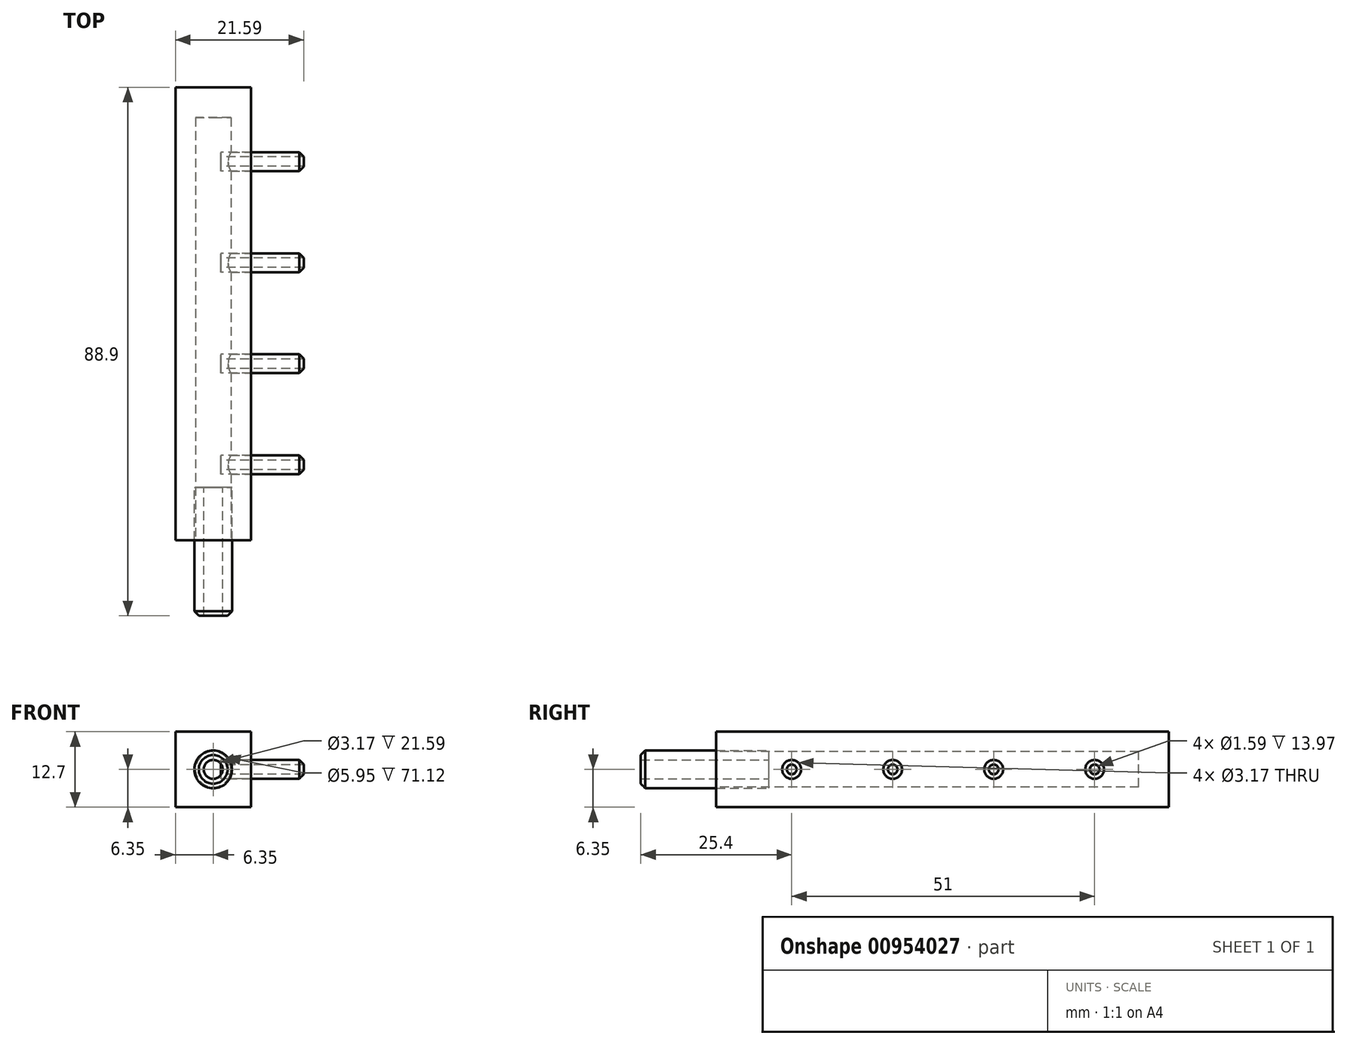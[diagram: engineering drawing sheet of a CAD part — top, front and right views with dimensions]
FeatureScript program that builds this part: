
annotation { "Feature Type Name" : "Feature", "Feature Type Description" : "" }
export const myFeature = defineFeature(function(context is Context, id is Id, definition is map)
    precondition{}
    {
        {
            var Q0;
            Q0=qCreatedBy(makeId("Front.planeOp"),FACE);
            var sketch = newSketch(context, id + "F0", { "sketchPlane" : qUnion([Q0])});
            skLineSegment(sketch, "E0.bottom", {"start": v(6.35, 6.35) * mm, "end": v(-6.35, 6.35) * mm});
            skLineSegment(sketch, "E0.top", {"start": v(6.35, -6.35) * mm, "end": v(-6.35, -6.35) * mm});
            skLineSegment(sketch, "E0.left", {"start": v(6.35, 6.35) * mm, "end": v(6.35, -6.35) * mm});
            skLineSegment(sketch, "E0.right", {"start": v(-6.35, 6.35) * mm, "end": v(-6.35, -6.35) * mm});
            skPoint(sketch, "E0.middle", {"position": v(0, 0) * mm});
            skSolve(sketch);
        }
        {
            var Q0;
            Q0 = qSketchRegion(id + "F0", true);
            extrude(context, id + "F1", {"entities" : qUnion([Q0]), "endBound" : BoundingType.SYMMETRIC, "depth" : 76.2 * mm, "offsetDistance" : 25.4 * mm});
        }
        {
            var Q0;
            Q0=makeQuery(id+"F1.opExtrude","CAP_FACE",FACE,{"disambiguationData":[OSD([sQuery(id+"F0.wireOp",EDGE,"E0.bottom"),sQuery(id+"F0.wireOp",EDGE,"E0.top"),sQuery(id+"F0.wireOp",EDGE,"E0.left"),sQuery(id+"F0.wireOp",EDGE,"E0.right")])],"isStart":false});
            var sketch = newSketch(context, id + "F2", { "sketchPlane" : qUnion([Q0])});
            skCircle(sketch, "E1", {"center": v(0, 0) * mm, "radius": 2.98 * mm});
            skSolve(sketch);
        }
        {
            var Q0;
            Q0 = qSketchRegion(id + "F2", true);
            extrude(context, id + "F3", {"entities" : qUnion([Q0]), "operationType" : NewBodyOperationType.REMOVE, "oppositeDirection" : true, "depth" : 71.12 * mm, "offsetDistance" : 25.4 * mm});
        }
        {
            var Q0;
            Q0=makeQuery(id+"F1.opExtrude","SWEPT_FACE",FACE,{"disambiguationData":[OSD([sQuery(id+"F0.wireOp",EDGE,"E0.left")])]});
            var sketch = newSketch(context, id + "F4", { "sketchPlane" : qUnion([Q0])});
            skCircle(sketch, "E2", {"center": v(-25.4, 0) * mm, "radius": 1.59 * mm});
            skCircle(sketch, "E3.1.0.0", {"center": v(-8.4, 0) * mm, "radius": 1.59 * mm});
            skCircle(sketch, "E3.2.0.0", {"center": v(8.6, 0) * mm, "radius": 1.59 * mm});
            skCircle(sketch, "E3.3.0.0", {"center": v(25.6, 0) * mm, "radius": 1.59 * mm});
            skLineSegment(sketch, "E3.direction1", {"start": v(-25.4, 0) * mm, "end": v(-8.4, 0) * mm, "construction": true});
            skSolve(sketch);
        }
        {
            var Q0;
            Q0 = qSketchRegion(id + "F4", true);
            extrude(context, id + "F5", {"entities" : qUnion([Q0]), "operationType" : NewBodyOperationType.REMOVE, "endBound" : BoundingType.UP_TO_NEXT, "oppositeDirection" : true, "depth" : 25.4 * mm, "offsetDistance" : 25.4 * mm});
        }
        {
            var Q0;
            Q0=makeQuery(id+"F1.opExtrude","CAP_FACE",FACE,{"disambiguationData":[OSD([sQuery(id+"F0.wireOp",EDGE,"E0.bottom"),sQuery(id+"F0.wireOp",EDGE,"E0.top"),sQuery(id+"F0.wireOp",EDGE,"E0.left"),sQuery(id+"F0.wireOp",EDGE,"E0.right")])],"isStart":false});
            var sketch = newSketch(context, id + "F6", { "sketchPlane" : qUnion([Q0])});
            skCircle(sketch, "E4", {"center": v(0, 0) * mm, "radius": 3.18 * mm});
            skCircle(sketch, "E5", {"center": v(0, 0) * mm, "radius": 1.59 * mm});
            skSolve(sketch);
        }
        {
            var Q0;
            Q0 = qSketchRegion(id + "F6", true);
            extrude(context, id + "F7", {"entities" : qUnion([Q0]), "depth" : 12.7 * mm, "offsetDistance" : 25.4 * mm, "hasSecondDirection" : true, "secondDirectionOppositeDirection" : true, "secondDirectionDepth" : 8.9 * mm});
        }
        {
            var Q0;
            Q0=makeQuery(id+"F1.opExtrude","SWEPT_FACE",FACE,{"disambiguationData":[OSD([sQuery(id+"F0.wireOp",EDGE,"E0.left")])]});
            var sketch = newSketch(context, id + "F8", { "sketchPlane" : qUnion([Q0])});
            skCircle(sketch, "E6", {"center": v(-25.4, 0) * mm, "radius": 1.59 * mm});
            skCircle(sketch, "E7", {"center": v(-8.4, 0) * mm, "radius": 1.59 * mm});
            skCircle(sketch, "E8", {"center": v(8.6, 0) * mm, "radius": 1.59 * mm});
            skCircle(sketch, "E9", {"center": v(25.6, 0) * mm, "radius": 1.59 * mm});
            skCircle(sketch, "E10", {"center": v(-25.4, 0) * mm, "radius": 0.8 * mm});
            skCircle(sketch, "E11", {"center": v(-8.4, 0) * mm, "radius": 0.8 * mm});
            skCircle(sketch, "E12", {"center": v(8.6, 0) * mm, "radius": 0.8 * mm});
            skCircle(sketch, "E13", {"center": v(25.6, 0) * mm, "radius": 0.8 * mm});
            skSolve(sketch);
        }
        {
            var Q0;
            Q0 = qSketchRegion(id + "F8", true);
            extrude(context, id + "F9", {"entities" : qUnion([Q0]), "depth" : 8.9 * mm, "offsetDistance" : 25.4 * mm, "hasSecondDirection" : true, "secondDirectionOppositeDirection" : true, "secondDirectionDepth" : 5.08 * mm});
        }
        {
            var Q0;
            Q0=makeQuery(id+"F7.opExtrude","CAP_EDGE",EDGE,{"disambiguationData":[OSD([sQuery(id+"F6.wireOp",EDGE,"E4")])],"isStart":false});
            var Q1;
            Q1=makeQuery(id+"F9.opExtrude","CAP_EDGE",EDGE,{"disambiguationData":[OSD([sQuery(id+"F8.wireOp",EDGE,"E6")])],"isStart":false});
            var Q2;
            Q2=makeQuery(id+"F9.opExtrude","CAP_EDGE",EDGE,{"disambiguationData":[OSD([sQuery(id+"F8.wireOp",EDGE,"E7")])],"isStart":false});
            var Q3;
            Q3=makeQuery(id+"F9.opExtrude","CAP_EDGE",EDGE,{"disambiguationData":[OSD([sQuery(id+"F8.wireOp",EDGE,"E8")])],"isStart":false});
            var Q4;
            Q4=makeQuery(id+"F9.opExtrude","CAP_EDGE",EDGE,{"disambiguationData":[OSD([sQuery(id+"F8.wireOp",EDGE,"E9")])],"isStart":false});
            chamfer(context, id + "F10", {"entities" : qUnion([Q0, Q1, Q2, Q3, Q4]), "width" : 0.76 * mm, "tangentPropagation" : true});
        }
    });
